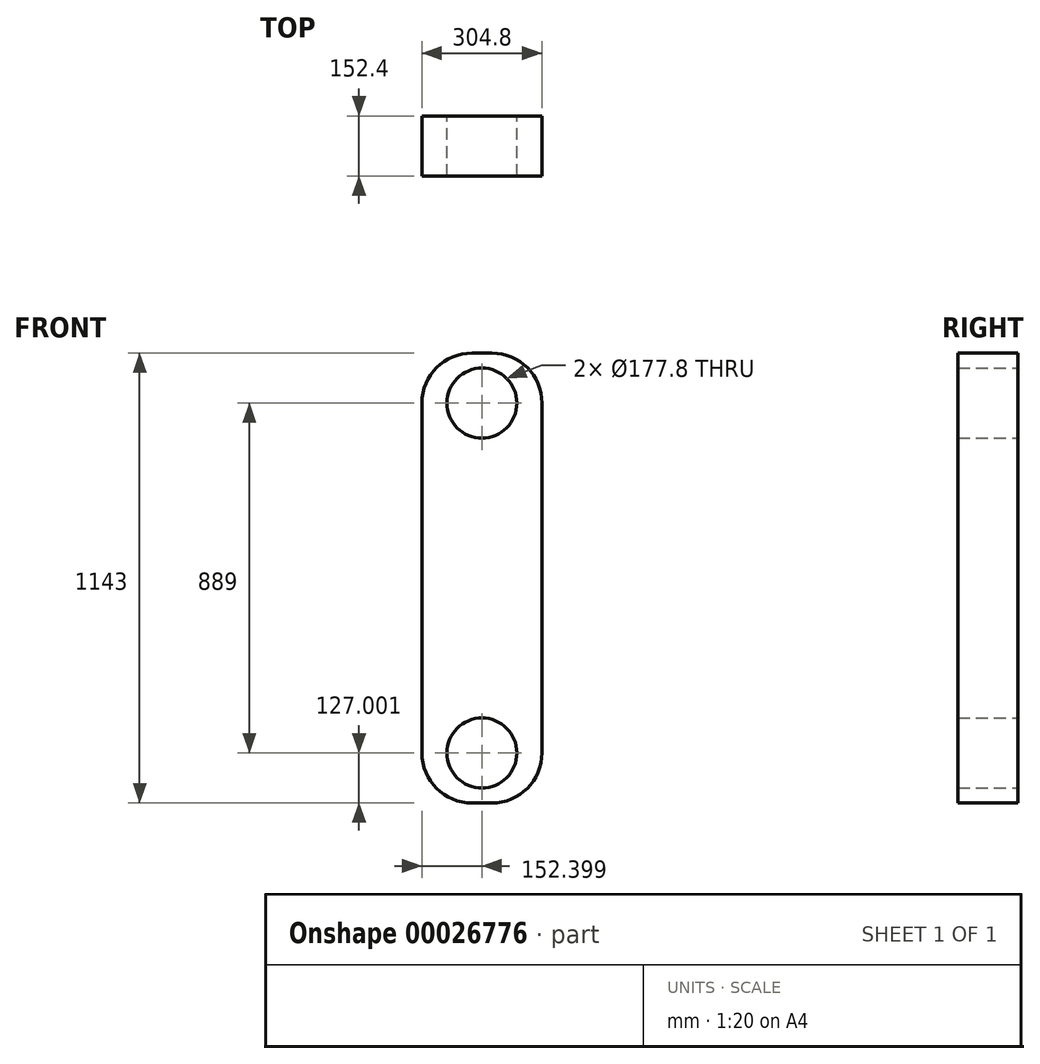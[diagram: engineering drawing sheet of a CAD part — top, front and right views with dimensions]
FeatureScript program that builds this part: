
annotation { "Feature Type Name" : "Feature", "Feature Type Description" : "" }
export const myFeature = defineFeature(function(context is Context, id is Id, definition is map)
    precondition{}
    {
        {
            var Q0;
            Q0=qCreatedBy(makeId("Front.planeOp"),FACE);
            var sketch = newSketch(context, id + "F0", { "sketchPlane" : qUnion([Q0])});
            skLineSegment(sketch, "E0", {"start": v(-731.17, 515.94) * mm, "end": v(-731.17, -373.06) * mm});
            skLineSegment(sketch, "E1", {"start": v(-604.17, -500.06) * mm, "end": v(-553.37, -500.06) * mm});
            skLineSegment(sketch, "E2", {"start": v(-426.37, -373.06) * mm, "end": v(-426.37, 515.94) * mm});
            skLineSegment(sketch, "E3", {"start": v(-604.17, 642.94) * mm, "end": v(-553.37, 642.94) * mm});
            skCircle(sketch, "E4", {"center": v(-578.77, -373.06) * mm, "radius": 88.9 * mm});
            skCircle(sketch, "E5", {"center": v(-578.77, 515.94) * mm, "radius": 88.9 * mm});
            skPoint(sketch, "E6.visualSharp", {"position": v(-731.17, 642.94) * mm});
            skArc(sketch, "E6.filletArc", {"start": v(-604.17, 642.94) * mm, "mid": v(-693.97, 605.74) * mm, "end": v(-731.17, 515.94) * mm});
            skPoint(sketch, "E7.visualSharp", {"position": v(-426.37, 642.94) * mm});
            skArc(sketch, "E7.filletArc", {"start": v(-426.37, 515.94) * mm, "mid": v(-463.57, 605.74) * mm, "end": v(-553.37, 642.94) * mm});
            skPoint(sketch, "E8.visualSharp", {"position": v(-426.37, -500.06) * mm});
            skArc(sketch, "E8.filletArc", {"start": v(-553.37, -500.06) * mm, "mid": v(-463.57, -462.86) * mm, "end": v(-426.37, -373.06) * mm});
            skPoint(sketch, "E9.visualSharp", {"position": v(-731.17, -500.06) * mm});
            skArc(sketch, "E9.filletArc", {"start": v(-731.17, -373.06) * mm, "mid": v(-693.97, -462.86) * mm, "end": v(-604.17, -500.06) * mm});
            skSolve(sketch);
        }
        {
            var Q0;
            Q0=makeQuery(id+"F0.imprint","IMPRINT",FACE,{"disambiguationData":[TD([[makeQuery(id+"F0.imprint","IMPRINT",EDGE,{"derivedFrom":sQuery(id+"F0.wireOp",EDGE,"E0")}),1.0]])]});
            extrude(context, id + "F1", {"entities" : qUnion([Q0]), "endBound" : BoundingType.SYMMETRIC, "depth" : 152.4 * mm});
        }
    });
